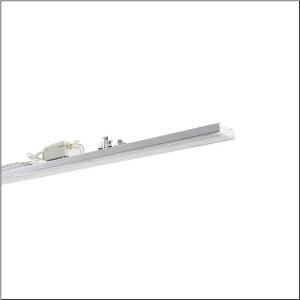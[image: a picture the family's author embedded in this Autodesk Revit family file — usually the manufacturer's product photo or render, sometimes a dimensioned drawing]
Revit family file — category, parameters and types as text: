
# Revit family: licross_21_recessed_mo_52tl1e7n485g
name_source: partatom
category: Lighting Fixtures
units: mm (PartAtom-declared; Revit-internal decimal feet)

## family parameters
Cut with Voids When Loaded = No
Host = Face
Light Source = No
Part Type = Normal
Room Calculation Point = No
Round Connector Dimension = Use Diameter
Shared = No

## types (1)
- Licross 21 Recessed MO (1 x LED, 8530 lm, 47.9 W, 4000K)
    Apparent Load = 48 VA
    CIE Flux Codes = 85 95 99 100 100
    Color Rendering = 80
    Color Temperature = 4000K
    Default Elevation = 1800 mm
    Description = Licross 21 Recessed MO, luminaire insert, of sheet steel, galvanised, coil coated, white, length: 1.500mm, width: 66mm, height: 67mm, LED rated luminous flux: 8.530lm, light colour: 840, SDCM (Standard Deviation of Colour Matching)MacAdam ≤ 3 SDCM (initial), control gear: ON/OFF, with plug, 3-pole, with phase selection, mains connection: 220..240V, AC, 50/60Hz, rated input power: 48W, internal wiring halogen-free, primary light control with lens, of plastic, primary optical cover: cover, of PMMA, light emission: direct distribution, primary light characteristic: symmetric, protection rating (complete): IP40, insulation class (complete): insulation class I (protective earthing), certification: CE, ENEC, VDE, UKCA, protection symbol: D if used in an environment without relevant dust loads with corresponding accessories, impact resistance: IK06, permissible ambient temperature for indoor applications: -35..+40°C, corresponds to IFS (International Featured Standards) requirements for safety and quality in the food industry, reducing of maximum allowable ambient temperature of 5°C with ceiling mounting, LABS conformity tested according to VDMA 24364:2018-05, The light source and the operating device comply with the requirements of the Ecodesign Regulation (EU) 2019/2020 and are replaceable in accordance with this regulation, packaging unit: 1 piece
    Height = 58 mm
    Lamp = 1 x LED
    Lamp Light Flux = 8530 lm
    Lamp Power = 47.9 W
    Lamp count = 1
    Length = 1500 mm
    Luminous efficacy = 178 lm/W
    Manufacturer = Siteco
    ModVariant = No
    Model = 52TL1E7N485G
    Mounting Place = Ceiling
    Mounting Type = Pendant
    Number of Poles = 1
    OnlyDefault = Yes
    Power Factor = 1
    Product Name = Licross 21 Recessed MO
    Product group = luminaire insert | ceiling pendant
    ProductGroupID = 901
    Protection Class = Protection class I
    Protection Degree = IP 40
    RLX_Detail_Level = 1
    RLX_Emergency_Light_Flux = 0 lm
    RLX_Emergency_Type = 0
    RLX_Emergency_Type_DB = No
    RlxData = <blob elided: 21253 chars, md5=b1e4777c>
    Socket = socket
    Standby Power = 0 W
    System Light Flux = 8530 lm
    System Power = 48 W
    Type Comments = Product without accessories
    Type Image = l_1296930.jpg
    URL = http://relux.com
    VarID = ---
    Voltage = 0 V
    Weight = 0.00 kg
    Width = 66 mm

## geometry (parser evidence)
native form markers: Blend x4, Sweep x13
no freeform markers — native parametric forms only
